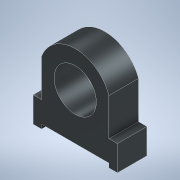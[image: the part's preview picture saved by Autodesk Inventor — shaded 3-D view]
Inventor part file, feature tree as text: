
AUTODESK INVENTOR PART (.ipt)
format: ipt  version: 2022.2 (Build 262287030, 287C)  size: 120,832 bytes
history: native  units: in
note: dims shown in document units (in); Inventor stores cm internally (conversion verified against a paired STEP export)
features: extrude x1, sketch x1
ambient origin geometry x8: Origin, YZ Plane, XZ Plane, XY Plane, X Axis, Y Axis, Z Axis, Center Point
bodies: Solid1 (feature_tree)
feature tree (2):
  extrude  "Extrusion1"  Depth=1.75in
  sketch  "Sketch1"  dims[d9=2.5in d10=3.0in d11=4.0in d12=0.5in d13=0.25in d14=1.5in d15=2.125in d16=1.75in d17=0.0in]
